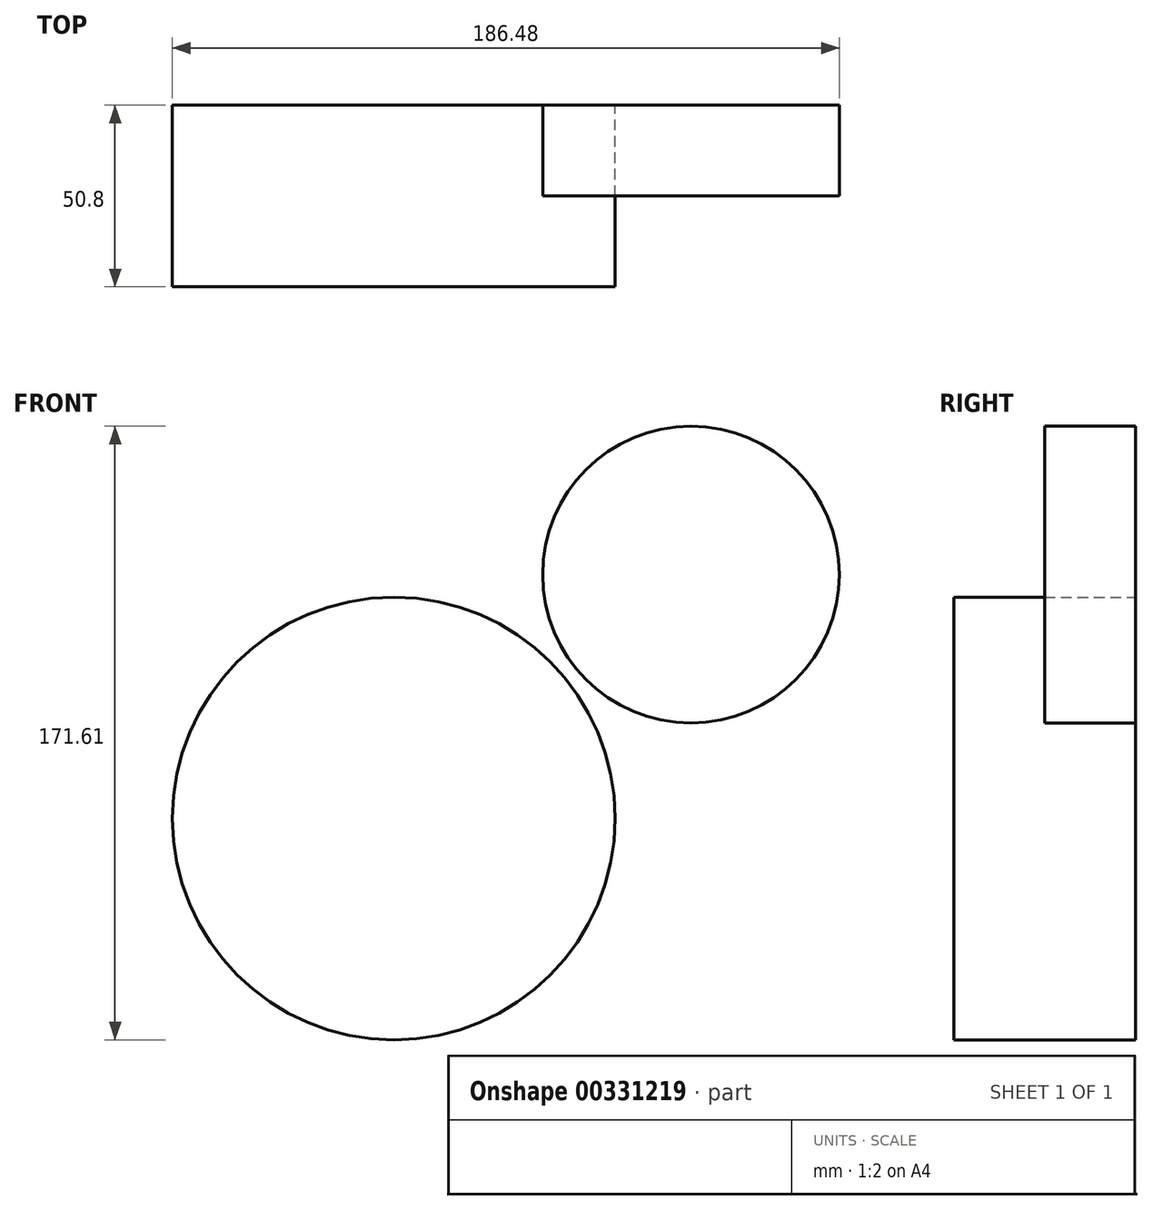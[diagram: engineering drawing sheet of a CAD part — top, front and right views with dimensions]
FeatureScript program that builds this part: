
annotation { "Feature Type Name" : "Feature", "Feature Type Description" : "" }
export const myFeature = defineFeature(function(context is Context, id is Id, definition is map)
    precondition{}
    {
        {
            var Q0;
            Q0=qCreatedBy(makeId("Front.planeOp"),FACE);
            var sketch = newSketch(context, id + "F0", { "sketchPlane" : qUnion([Q0])});
            skCircle(sketch, "E0", {"center": v(0, 0) * mm, "radius": 61.9 * mm});
            skCircle(sketch, "E1", {"center": v(83.1, 68.23) * mm, "radius": 41.48 * mm});
            skLineSegment(sketch, "E2", {"start": v(42.44, 45.07) * mm, "end": v(103.72, 104.21) * mm});
            skSolve(sketch);
        }
        {
            var Q0;
            Q0 = qSketchRegion(id + "F0", true);
            extrude(context, id + "F1", {"entities" : qUnion([Q0]), "depth" : 25.4 * mm});
        }
        {
            var Q0;
            Q0=makeQuery(id+"F1.opExtrude","CAP_FACE",FACE,{"disambiguationData":[OSD([sQuery(id+"F0.wireOp",EDGE,"E0")])],"isStart":false});
            extrude(context, id + "F2", {"entities" : qUnion([Q0]), "operationType" : NewBodyOperationType.ADD, "depth" : 25.4 * mm});
        }
    });
